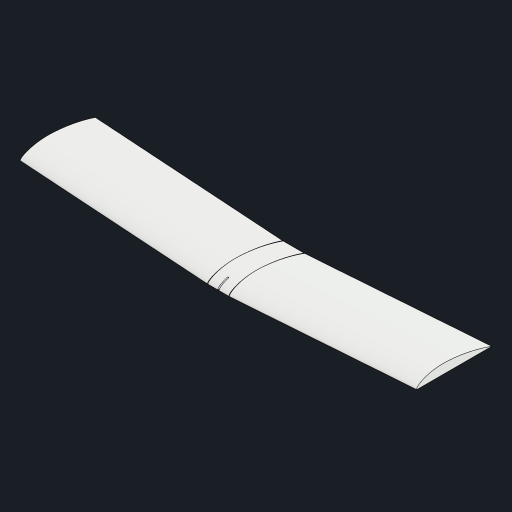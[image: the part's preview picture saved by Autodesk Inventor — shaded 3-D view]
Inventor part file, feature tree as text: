
AUTODESK INVENTOR PART (.ipt)
format: ipt  version: 2023 (Build 270158000, 158)  size: 209,408 bytes
history: native  units: mm
features: sketch x4, extrude x3, other x2, projected_geometry x2, revolve x1, mirror x1
ambient origin geometry x8: Origin, YZ Plane, XZ Plane, XY Plane, X Axis, Y Axis, Z Axis, Center Point
bodies: Body1 (feature_tree)
feature tree (13):
  other  "ソリッド1"
  extrude  "押し出し1"  Depth=25.0mm TaperAngle=0.0deg
  revolve  "回転1"
  extrude  "押し出し3"  Depth=0.698132mm
  mirror  "ミラー4"
  extrude  "押し出し4"  Depth=180.0mm
  sketch  "スケッチ1"
  sketch  "スケッチ7"
  projected_geometry  "投影ループ2"
  sketch  "スケッチ9"
  projected_geometry  "投影ループ4"
  sketch  "スケッチ11"
  other  "断面エッジを投影3"
